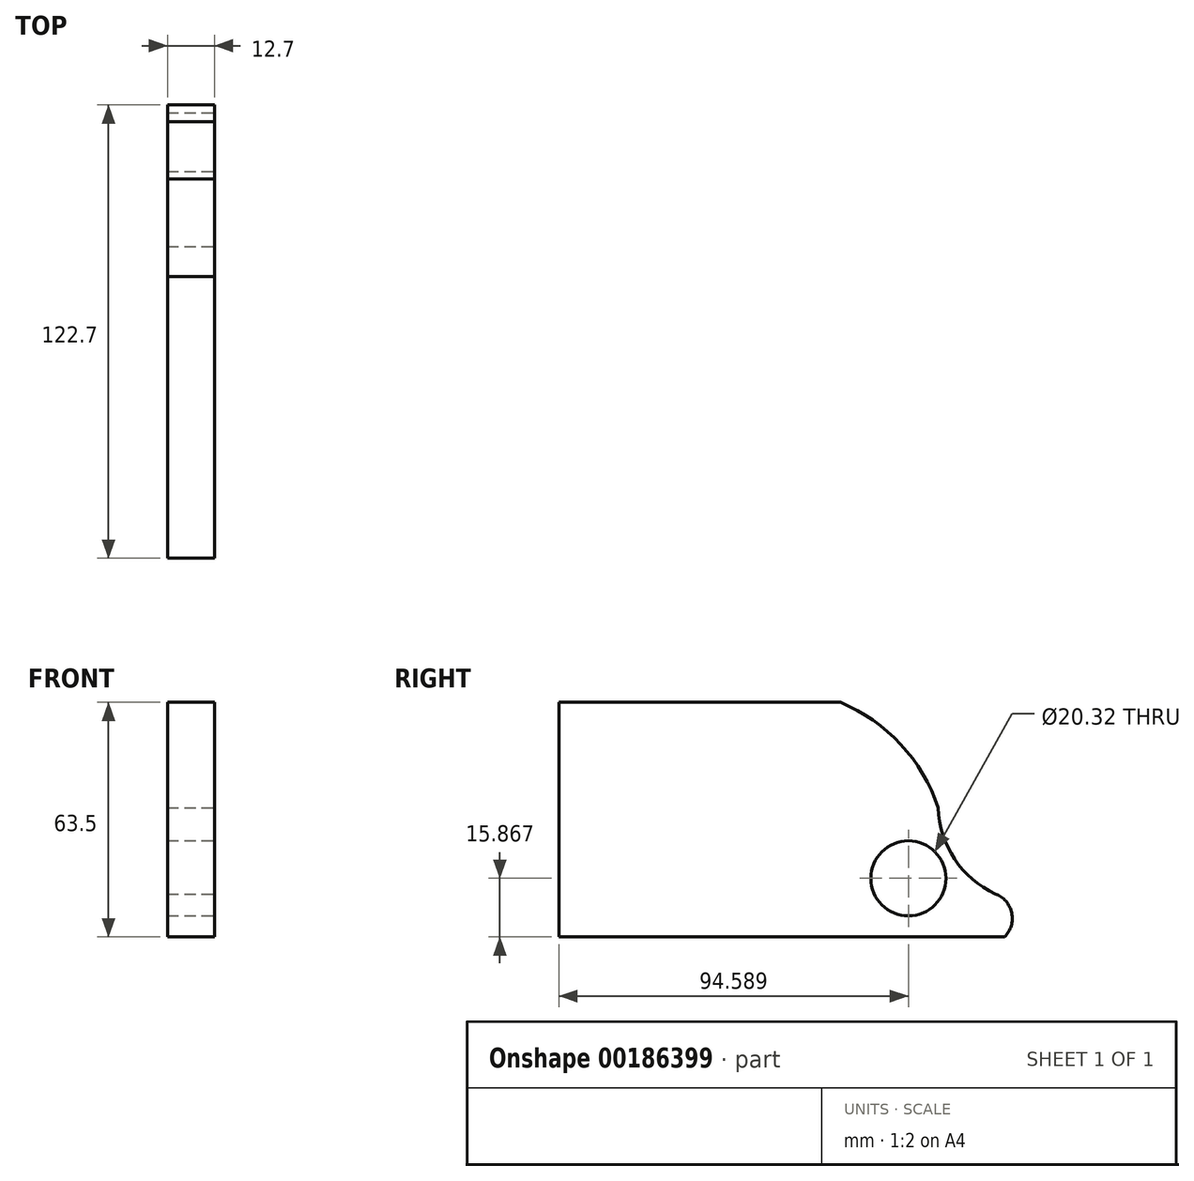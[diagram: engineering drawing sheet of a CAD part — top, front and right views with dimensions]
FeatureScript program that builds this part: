
annotation { "Feature Type Name" : "Feature", "Feature Type Description" : "" }
export const myFeature = defineFeature(function(context is Context, id is Id, definition is map)
    precondition{}
    {
        {
            var Q0;
            Q0=qCreatedBy(makeId("Right.planeOp"),FACE);
            var sketch = newSketch(context, id + "F0", { "sketchPlane" : qUnion([Q0])});
            skLineSegment(sketch, "E0.bottom", {"start": v(-42.51, 51.84) * mm, "end": v(33.69, 51.84) * mm});
            skLineSegment(sketch, "E0.top", {"start": v(-42.51, -11.66) * mm, "end": v(33.69, -11.66) * mm});
            skLineSegment(sketch, "E0.left", {"start": v(-42.51, 51.84) * mm, "end": v(-42.51, -11.66) * mm});
            skLineSegment(sketch, "E0.right", {"start": v(33.69, 51.84) * mm, "end": v(33.69, -11.66) * mm});
            skArc(sketch, "E1", {"start": v(60.12, 23.3) * mm, "mid": v(50.02, 40.46) * mm, "end": v(33.69, 51.84) * mm});
            skArc(sketch, "E2", {"start": v(60.12, 23.3) * mm, "mid": v(64.57, 9.46) * mm, "end": v(75.6, 0) * mm});
            skArc(sketch, "E3", {"start": v(78.11, -11.66) * mm, "mid": v(80.03, -5.15) * mm, "end": v(75.6, 0) * mm});
            skLineSegment(sketch, "E4", {"start": v(33.69, -11.66) * mm, "end": v(78.11, -11.66) * mm});
            skCircle(sketch, "E5", {"center": v(52.08, 4.2) * mm, "radius": 10.16 * mm});
            skSolve(sketch);
        }
        {
            var Q0;
            Q0 = qSketchRegion(id + "F0", true);
            var Q1;
            Q1=makeQuery(id+"F0.imprint","IMPRINT",FACE,{"disambiguationData":[TD([[makeQuery(id+"F0.imprint","IMPRINT",EDGE,{"derivedFrom":sQuery(id+"F0.wireOp",EDGE,"E0.bottom")}),-1.0]])]});
            extrude(context, id + "F1", {"entities" : qUnion([Q0, Q1]), "oppositeDirection" : true, "depth" : 12.7 * mm});
        }
    });
